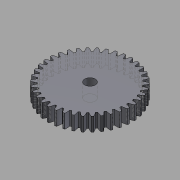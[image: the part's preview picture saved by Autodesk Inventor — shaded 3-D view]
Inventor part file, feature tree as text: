
AUTODESK INVENTOR PART (.ipt)
format: ipt  version: 2015 (Build 190159000, 159)  size: 302,592 bytes
history: native  units: mm (DEFAULTED — no unit token found)
features: plane x3, other x3, sketch x3, extrude x2
ambient origin geometry x8: Origin, YZ Plane, XZ Plane, XY Plane, X Axis, Y Axis, Z Axis, Center Point
bodies: Solid1 (feature_tree)
feature tree (11):
  extrude  "Extrusion1"  Depth=3.3mm TaperAngle=0.0deg
  plane  "Work Plane2"
  plane  "Work Plane8"
  plane  "Work Plane9"
  other  "Spur Gear"
  extrude  "Extrusion2"  Depth=10.0mm TaperAngle=0.0deg
  sketch  "Sketch1"  dims[d0=20.0mm d1=3.3mm d2=0.0mm]
  sketch  "Sketch2"  dims[d3=19.0mm d4=10.0mm d5=0.0mm]
  other  "Srf1"
  sketch  "Sketch3"  dims[d16=12.0mm d17=0.0mm d34=0.826735mm d39=0.0mm d41=0.0mm d43=12.0mm d46=12.0mm d47=0.0mm d48=0.0mm d49=2.5mm d50=10.0mm d51=0.0mm]
  other  "Pitch Diameter"
